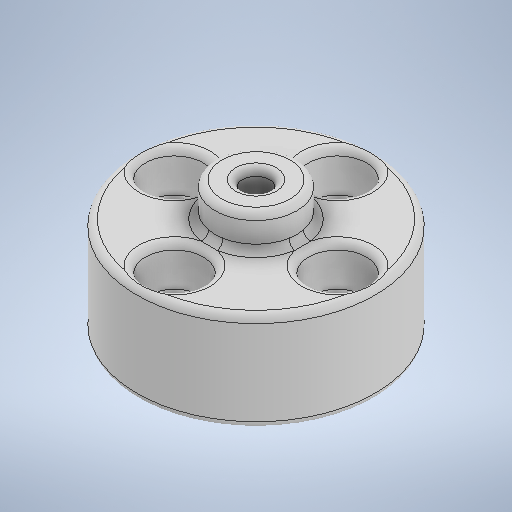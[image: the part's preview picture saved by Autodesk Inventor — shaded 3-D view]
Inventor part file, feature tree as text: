
AUTODESK INVENTOR PART (.ipt)
format: ipt  version: 2025.1 (Build 291241000, 241)  size: 390,144 bytes
history: native  units: mm
features: sketch x5, extrude x4, other x3, hole x1, fillet x1
ambient origin geometry x8: Origin, YZ Plane, XZ Plane, XY Plane, X Axis, Y Axis, Z Axis, Center Point
bodies: Solide1 (feature_tree)
feature tree (14):
  extrude  "Extrusion1"  Depth=35.0mm
  extrude  "Extrusion2"  Depth=24.0mm
  extrude  "Extrusion4"  Depth=4.0mm
  extrude  "Extrusion3"  Depth=14.5mm TaperAngle=0.0deg
  hole  "Perçage1"  [1 undecoded]
  fillet  "Congé2"  Radius=8.5mm
  sketch  "Esquisse1"
  sketch  "Esquisse2"
  other  "Réseau d'esquisse circulaire2"
  other  "Réseau d'esquisse circulaire3"
  sketch  "Esquisse3"
  sketch  "Esquisse5"
  sketch  "Esquisse6"
  other  "Réseau d'esquisse circulaire5"
note: 1 required parameter value undecoded (feature->parameter linkage not recoverable at this tier; creation-order binding heuristic only, values carry confidence <= 0.55)
